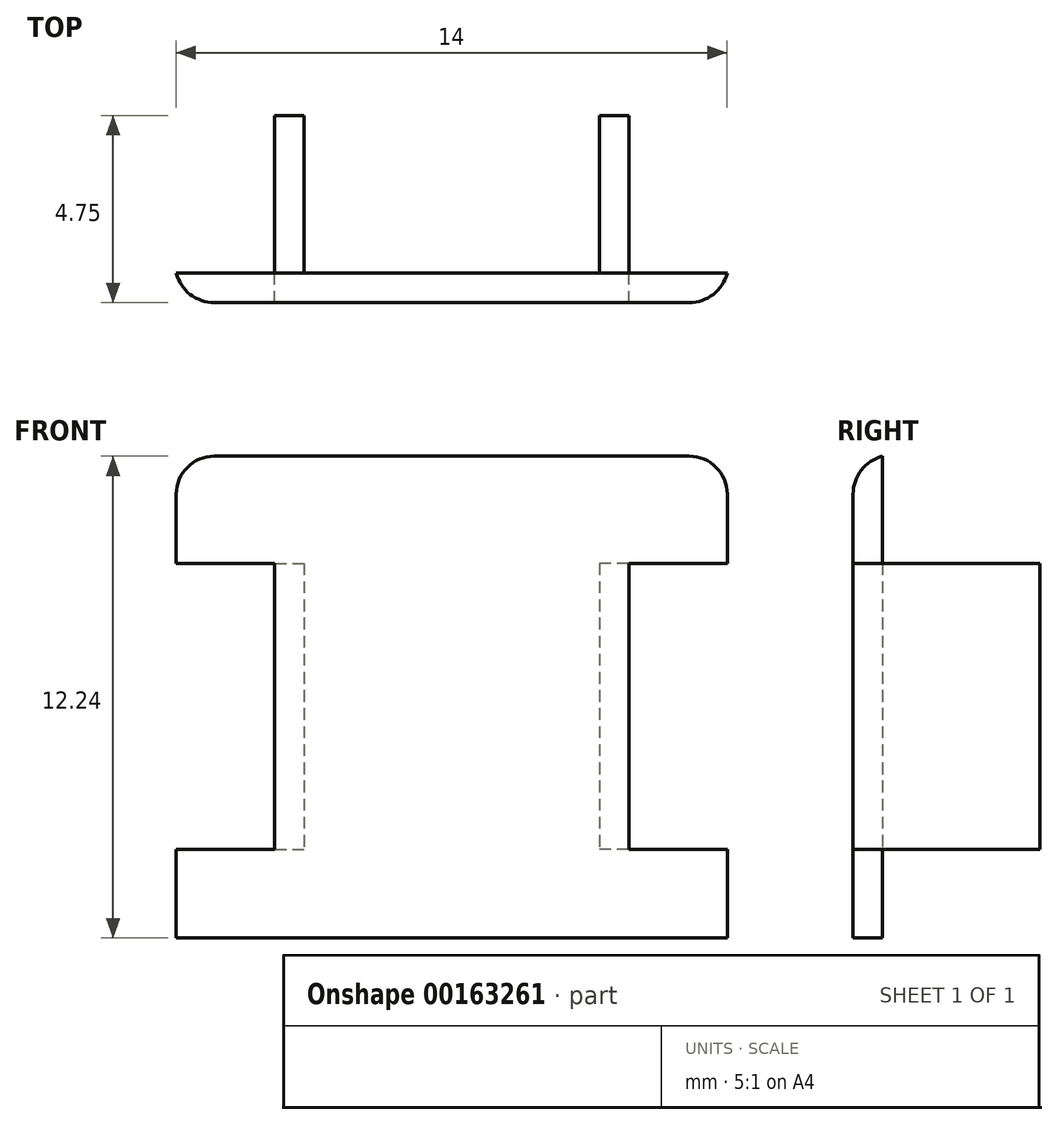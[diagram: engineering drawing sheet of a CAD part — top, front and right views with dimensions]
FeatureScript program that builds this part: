
annotation { "Feature Type Name" : "Feature", "Feature Type Description" : "" }
export const myFeature = defineFeature(function(context is Context, id is Id, definition is map)
    precondition{}
    {
        {
            var Q0;
            Q0=qCreatedBy(makeId("Top.planeOp"),FACE);
            var sketch = newSketch(context, id + "F0", { "sketchPlane" : qUnion([Q0])});
            skLineSegment(sketch, "E0", {"start": v(-12.42, 3.7) * mm, "end": v(1.58, 3.7) * mm});
            skArc(sketch, "E1", {"start": v(-12.42, 3.7) * mm, "mid": v(-12.06, 3.16) * mm, "end": v(-11.45, 2.95) * mm});
            skArc(sketch, "E2", {"start": v(0.61, 2.95) * mm, "mid": v(1.23, 3.16) * mm, "end": v(1.58, 3.7) * mm});
            skLineSegment(sketch, "E3", {"start": v(-11.45, 2.95) * mm, "end": v(0.61, 2.95) * mm});
            skSolve(sketch);
        }
        {
            var Q0;
            Q0 = qSketchRegion(id + "F0", true);
            extrude(context, id + "F1", {"entities" : qUnion([Q0]), "depth" : (10 + 2.27) * mm});
        }
        {
            var Q0;
            Q0=makeQuery(id+"F1.opExtrude","CAP_EDGE",EDGE,{"disambiguationData":[OSD([sQuery(id+"F0.wireOp",EDGE,"E3")])],"isStart":false});
            fillet(context, id + "F2", {"entities" : qUnion([Q0]), "radius" : 1 * mm, "tangentPropagation" : true, "allowEdgeOverflow" : false});
        }
        {
            var Q0;
            Q0=makeQuery(id+"F1.opExtrude","SWEPT_FACE",FACE,{"disambiguationData":[OSD([sQuery(id+"F0.wireOp",EDGE,"E0")])]});
            var sketch = newSketch(context, id + "F3", { "sketchPlane" : qUnion([Q0])});
            skLineSegment(sketch, "E4.bottom", {"start": v(12.42, 9.52) * mm, "end": v(9.92, 9.52) * mm});
            skLineSegment(sketch, "E4.top", {"start": v(12.42, 2.25) * mm, "end": v(9.92, 2.25) * mm});
            skLineSegment(sketch, "E4.left", {"start": v(12.42, 9.52) * mm, "end": v(12.42, 2.25) * mm});
            skLineSegment(sketch, "E4.right", {"start": v(9.92, 9.52) * mm, "end": v(9.92, 2.25) * mm});
            skLineSegment(sketch, "E5", {"start": v(5.42, 12.24) * mm, "end": v(5.42, 0) * mm, "construction": true});
            skLineSegment(sketch, "E6.MirrorCS", {"start": v(0.92, 9.52) * mm, "end": v(0.92, 2.25) * mm});
            skLineSegment(sketch, "E7.MirrorCS", {"start": v(-1.58, 9.52) * mm, "end": v(-1.58, 2.25) * mm});
            skLineSegment(sketch, "E8.MirrorCS", {"start": v(-1.58, 2.25) * mm, "end": v(0.92, 2.25) * mm});
            skLineSegment(sketch, "E9.MirrorCS", {"start": v(-1.58, 9.52) * mm, "end": v(0.92, 9.52) * mm});
            skSolve(sketch);
        }
        {
            var Q0;
            Q0 = qSketchRegion(id + "F3", true);
            extrude(context, id + "F4", {"entities" : qUnion([Q0]), "operationType" : NewBodyOperationType.REMOVE, "endBound" : BoundingType.THROUGH_ALL, "oppositeDirection" : true, "depth" : 25 * mm});
        }
        {
            var Q0;
            Q0=makeQuery(id+"F1.opExtrude","SWEPT_FACE",FACE,{"disambiguationData":[OSD([sQuery(id+"F0.wireOp",EDGE,"E0")])]});
            var sketch = newSketch(context, id + "F5", { "sketchPlane" : qUnion([Q0])});
            skLineSegment(sketch, "E10.bottom", {"start": v(0.92, 9.52) * mm, "end": v(1.67, 9.52) * mm});
            skLineSegment(sketch, "E10.top", {"start": v(0.92, 2.25) * mm, "end": v(1.67, 2.25) * mm});
            skLineSegment(sketch, "E10.left", {"start": v(0.92, 9.52) * mm, "end": v(0.92, 2.25) * mm});
            skLineSegment(sketch, "E10.right", {"start": v(1.67, 9.52) * mm, "end": v(1.67, 2.25) * mm});
            skLineSegment(sketch, "E11", {"start": v(5.42, 12.24) * mm, "end": v(5.42, 0) * mm, "construction": true});
            skLineSegment(sketch, "E12.MirrorCS", {"start": v(9.92, 9.52) * mm, "end": v(9.17, 9.52) * mm});
            skLineSegment(sketch, "E13.MirrorCS", {"start": v(9.17, 9.52) * mm, "end": v(9.17, 2.25) * mm});
            skLineSegment(sketch, "E14.MirrorCS", {"start": v(9.92, 9.52) * mm, "end": v(9.92, 2.25) * mm});
            skLineSegment(sketch, "E15.MirrorCS", {"start": v(9.92, 2.25) * mm, "end": v(9.17, 2.25) * mm});
            skSolve(sketch);
        }
        {
            var Q0;
            Q0 = qSketchRegion(id + "F5", true);
            extrude(context, id + "F6", {"entities" : qUnion([Q0]), "operationType" : NewBodyOperationType.ADD, "depth" : 4 * mm});
        }
    });
